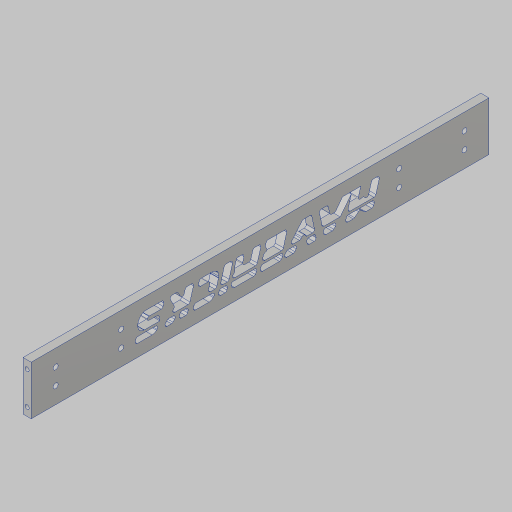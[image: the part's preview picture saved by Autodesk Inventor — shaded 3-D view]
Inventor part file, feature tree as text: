
AUTODESK INVENTOR PART (.ipt)
format: ipt  version: 2023.5 (Build 275446000, 446)  size: 552,448 bytes
history: native  units: in
note: dims shown in document units (in); Inventor stores cm internally (conversion verified against a paired STEP export)
features: sketch x4, hole x2, mirror x2, extrude x1, emboss x1, fillet x1
ambient origin geometry x8: Origin, YZ Plane, XZ Plane, XY Plane, X Axis, Y Axis, Z Axis, Center Point
bodies: Solid1 (feature_tree)
feature tree (11):
  extrude  "Extrusion1"  Depth=14.0in
  hole  "Hole2"  [1 undecoded]
  mirror  "Mirror1"
  hole  "Hole3"  [1 undecoded]
  mirror  "Mirror2"
  emboss  "Emboss1"
  fillet  "Fillet1"  Radius=0.5in
  sketch  "Sketch1"  dims[d1=1.5in d2=14.0in]
  sketch  "Sketch3"  dims[d3=0.25in d4=0.0in d20=0.25in]
  sketch  "Sketch4"  dims[d21=0.25in]
  sketch  "Sketch5"  dims[d22=0.13in d23=0.328in d24=0.332in d25=0.25in d26=0.5635in d27=0.5in d28=0.8108in d29=2.0in d30=0.5in d31=1.748in d32=0.156in d33=0.38in d34=0.385in d35=0.25in d36=0.5635in d37=1.0in d38=0.8108in d39=0.25in d40=0.0in d41=0.0625in]
note: 2 required parameter values undecoded (feature->parameter linkage not recoverable at this tier; creation-order binding heuristic only, values carry confidence <= 0.55)
